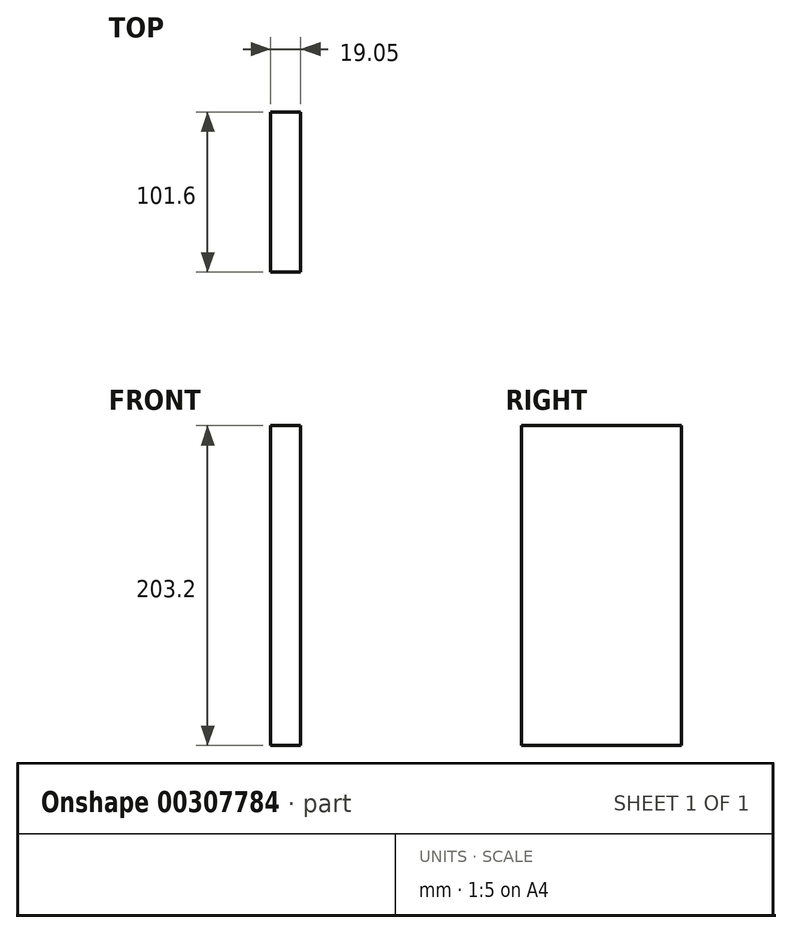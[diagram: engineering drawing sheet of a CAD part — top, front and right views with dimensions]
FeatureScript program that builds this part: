
annotation { "Feature Type Name" : "Feature", "Feature Type Description" : "" }
export const myFeature = defineFeature(function(context is Context, id is Id, definition is map)
    precondition{}
    {
        {
            var Q0;
            Q0=qCreatedBy(makeId("Right.planeOp"),FACE);
            var sketch = newSketch(context, id + "F0", { "sketchPlane" : qUnion([Q0])});
            skLineSegment(sketch, "E0.bottom", {"start": v(50.8, 101.6) * mm, "end": v(-50.8, 101.6) * mm});
            skLineSegment(sketch, "E0.top", {"start": v(50.8, -101.6) * mm, "end": v(-50.8, -101.6) * mm});
            skLineSegment(sketch, "E0.left", {"start": v(50.8, 101.6) * mm, "end": v(50.8, -101.6) * mm});
            skLineSegment(sketch, "E0.right", {"start": v(-50.8, 101.6) * mm, "end": v(-50.8, -101.6) * mm});
            skPoint(sketch, "E0.middle", {"position": v(0, 0) * mm});
            skSolve(sketch);
        }
        {
            var Q0;
            Q0=makeQuery(id+"F0.imprint","IMPRINT",FACE,{"disambiguationData":[TD([[makeQuery(id+"F0.imprint","IMPRINT",EDGE,{"derivedFrom":sQuery(id+"F0.wireOp",EDGE,"E0.bottom")}),1.0]])]});
            extrude(context, id + "F1", {"entities" : qUnion([Q0]), "depth" : 19.05 * mm});
        }
    });
